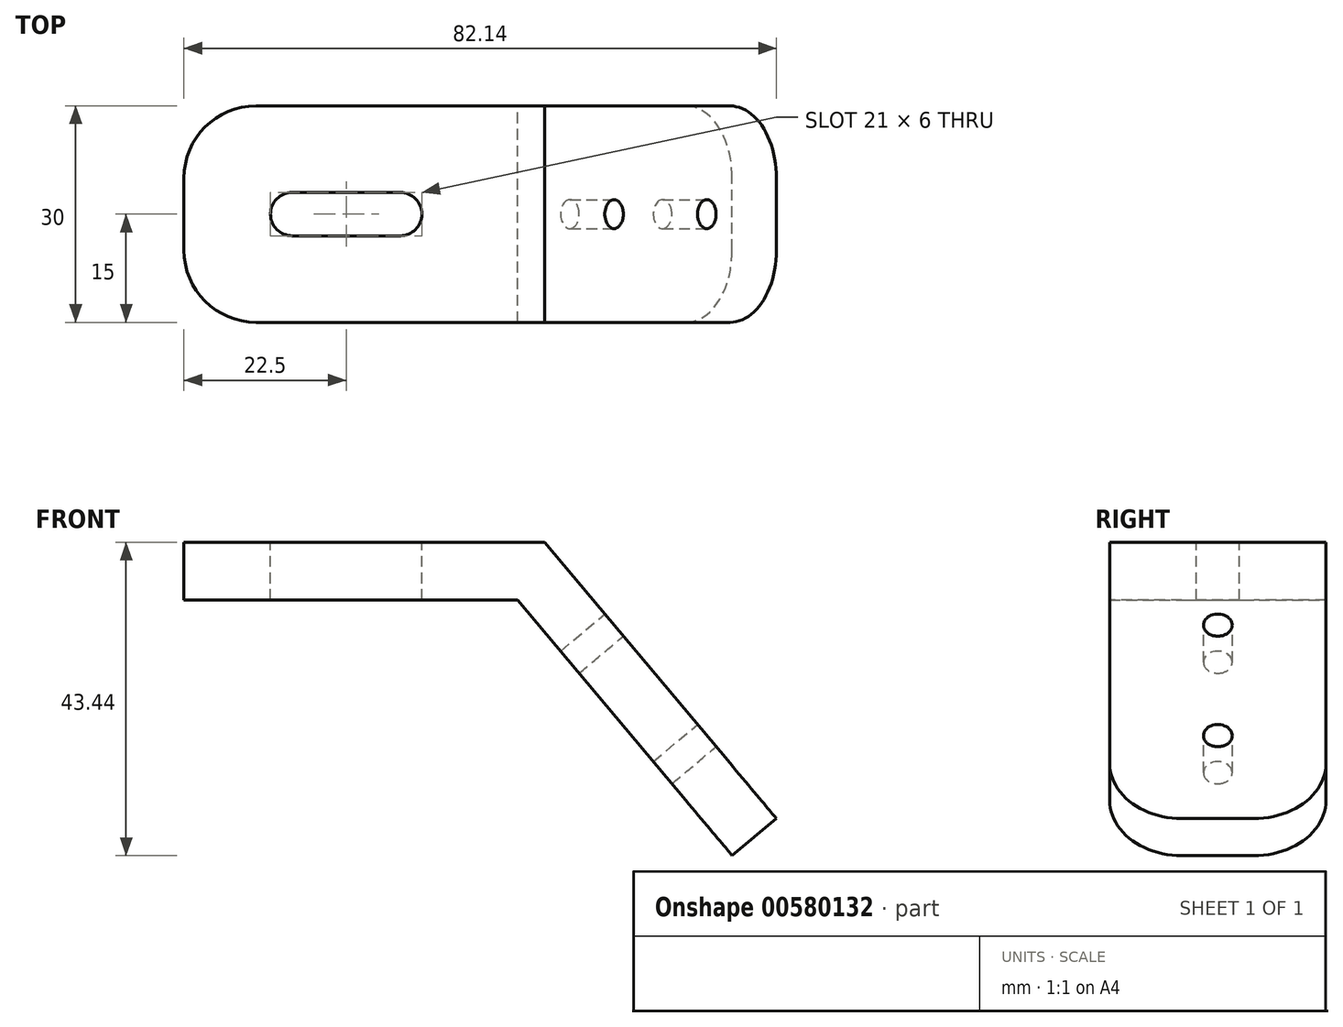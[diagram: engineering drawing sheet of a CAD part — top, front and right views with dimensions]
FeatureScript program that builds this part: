
annotation { "Feature Type Name" : "Feature", "Feature Type Description" : "" }
export const myFeature = defineFeature(function(context is Context, id is Id, definition is map)
    precondition{}
    {
        {
            var Q0;
            Q0=qCreatedBy(makeId("Front.planeOp"),FACE);
            var sketch = newSketch(context, id + "F0", { "sketchPlane" : qUnion([Q0])});
            skLineSegment(sketch, "E0", {"start": v(0, 0) * mm, "end": v(46.27, 0) * mm});
            skLineSegment(sketch, "E1", {"start": v(46.27, 0) * mm, "end": v(76.01, -35.44) * mm});
            skLineSegment(sketch, "E2.0", {"start": v(50, 8) * mm, "end": v(82.14, -30.3) * mm});
            skLineSegment(sketch, "E2.1", {"start": v(0, 8) * mm, "end": v(50, 8) * mm});
            skLineSegment(sketch, "E3", {"start": v(0, 0) * mm, "end": v(0, 8) * mm});
            skLineSegment(sketch, "E4", {"start": v(76.01, -35.44) * mm, "end": v(82.14, -30.3) * mm});
            skSolve(sketch);
        }
        {
            var Q0;
            Q0=makeQuery(id+"F0.imprint","IMPRINT",FACE,{"disambiguationData":[TD([[makeQuery(id+"F0.imprint","IMPRINT",EDGE,{"derivedFrom":sQuery(id+"F0.wireOp",EDGE,"E0")}),1.0]])]});
            extrude(context, id + "F1", {"entities" : qUnion([Q0]), "endBound" : BoundingType.SYMMETRIC, "depth" : 30 * mm, "offsetDistance" : 25 * mm});
        }
        {
            var Q0;
            Q0=makeQuery(id+"F1.opExtrude","SWEPT_FACE",FACE,{"disambiguationData":[OSD([sQuery(id+"F0.wireOp",EDGE,"E2.1")])]});
            var sketch = newSketch(context, id + "F2", { "sketchPlane" : qUnion([Q0])});
            skLineSegment(sketch, "E5", {"start": v(15, 0) * mm, "end": v(30, 0) * mm});
            skArc(sketch, "E6.0.startCap", {"start": v(15, -3) * mm, "mid": v(12, 0) * mm, "end": v(15, 3) * mm});
            skArc(sketch, "E6.0.endCap", {"start": v(30, 3) * mm, "mid": v(33, 0) * mm, "end": v(30, -3) * mm});
            skLineSegment(sketch, "E6.0.left", {"start": v(15, 3) * mm, "end": v(30, 3) * mm});
            skLineSegment(sketch, "E6.0.right", {"start": v(15, -3) * mm, "end": v(30, -3) * mm});
            skSolve(sketch);
        }
        {
            var Q0;
            Q0 = qSketchRegion(id + "F2", true);
            extrude(context, id + "F3", {"entities" : qUnion([Q0]), "operationType" : NewBodyOperationType.REMOVE, "endBound" : BoundingType.THROUGH_ALL, "oppositeDirection" : true, "depth" : 25 * mm, "offsetDistance" : 25 * mm});
        }
        {
            var Q0;
            Q0=makeQuery(id+"F1.opExtrude","SWEPT_FACE",FACE,{"disambiguationData":[OSD([sQuery(id+"F0.wireOp",EDGE,"E2.0")])]});
            var sketch = newSketch(context, id + "F4", { "sketchPlane" : qUnion([Q0])});
            skPoint(sketch, "E7", {"position": v(0, -41.01) * mm});
            skPoint(sketch, "E8", {"position": v(0, -61.01) * mm});
            skSolve(sketch);
        }
        {
            var Q0;
            Q0=sQuery(id+"F4.wireOp",VERTEX,"E7");
            var Q1;
            Q1=sQuery(id+"F4.wireOp",VERTEX,"E8");
            var Q2;
            Q2=makeQuery(id+"F1.opExtrude","SWEPT_BODY",BODY,{"disambiguationData":[OSD([sQuery(id+"F0.wireOp",EDGE,"E0"),sQuery(id+"F0.wireOp",EDGE,"E1"),sQuery(id+"F0.wireOp",EDGE,"E2.0"),sQuery(id+"F0.wireOp",EDGE,"E2.1"),sQuery(id+"F0.wireOp",EDGE,"E3"),sQuery(id+"F0.wireOp",EDGE,"E4")])]});
            hole(context, id + "F5", {"style" : HoleStyle.SIMPLE, "endStyle" : HoleEndStyle.THROUGH, "holeDiameter" : 4 * mm, "majorDiameter" : 5 * mm, "isTappedThrough" : true, "tappedDepth" : 12 * mm, "tapClearance" : 3, "locations" : qUnion([Q0, Q1]), "scope" : qUnion([Q2])});
        }
        {
            var Q0;
            Q0=makeQuery(id+"F1.opExtrude","CAP_EDGE",EDGE,{"disambiguationData":[OSD([sQuery(id+"F0.wireOp",EDGE,"E4")])],"isStart":false});
            var Q1;
            Q1=makeQuery(id+"F1.opExtrude","CAP_EDGE",EDGE,{"disambiguationData":[OSD([sQuery(id+"F0.wireOp",EDGE,"E4")])],"isStart":true});
            var Q2;
            Q2=makeQuery(id+"F1.opExtrude","CAP_EDGE",EDGE,{"disambiguationData":[OSD([sQuery(id+"F0.wireOp",EDGE,"E3")])],"isStart":false});
            var Q3;
            Q3=makeQuery(id+"F1.opExtrude","CAP_EDGE",EDGE,{"disambiguationData":[OSD([sQuery(id+"F0.wireOp",EDGE,"E3")])],"isStart":true});
            fillet(context, id + "F6", {"entities" : qUnion([Q0, Q1, Q2, Q3]), "radius" : 10 * mm, "tangentPropagation" : true, "allowEdgeOverflow" : false});
        }
    });
